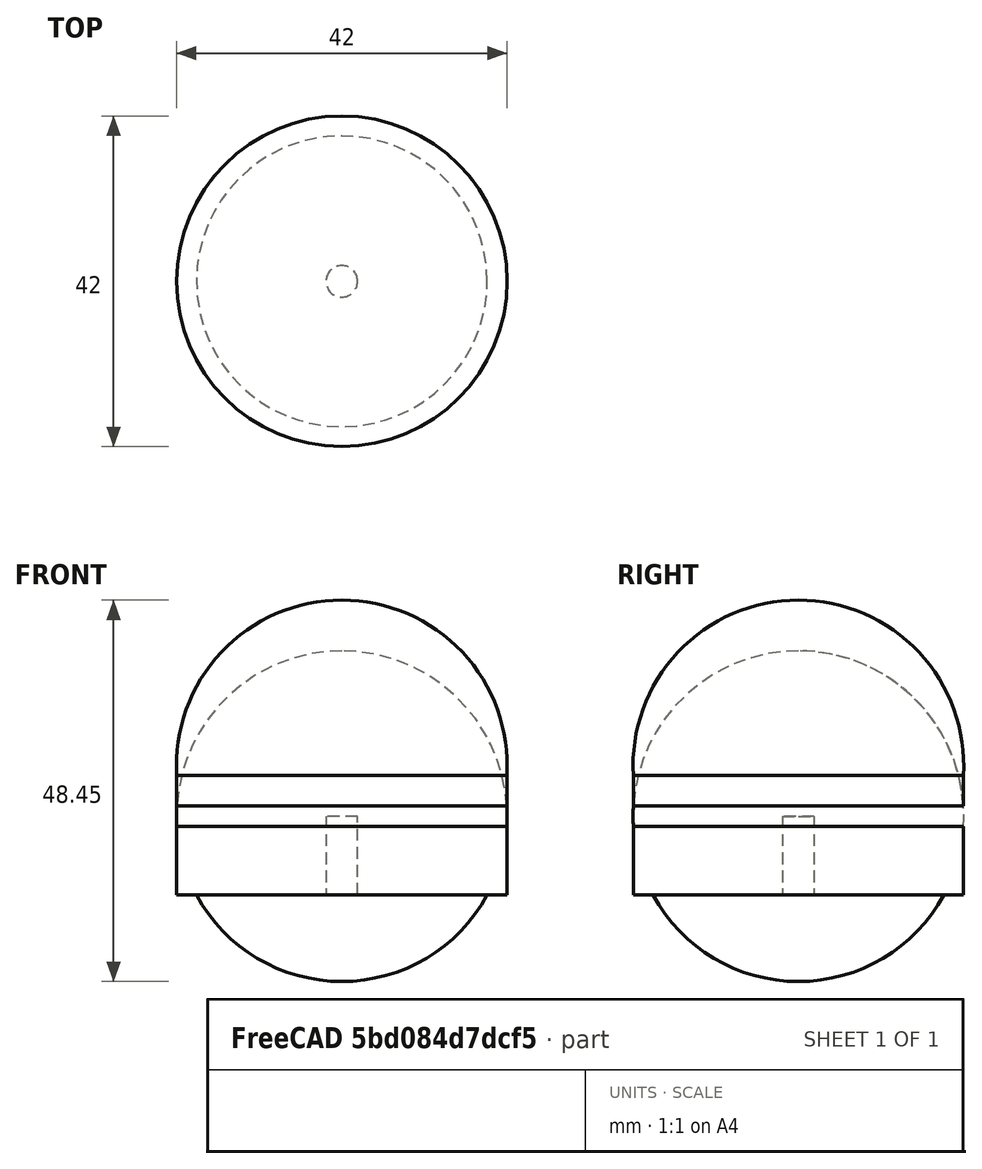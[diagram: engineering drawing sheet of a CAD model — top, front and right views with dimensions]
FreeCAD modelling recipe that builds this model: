
FCSTD DOCUMENT  (FreeCAD 1.0R39319 (Git))
Label: Final_looking_GOOD
License: Public Domain
LicenseURL: https://en.wikipedia.org/wiki/Public_domain
objects: Part::Cylinder×4, PartDesign::AdditiveSphere×2, Sketcher::SketchObject×1, PartDesign::Pad×1, PartDesign::Body×1, App::Part×1, Part::Cut×1
note: 17 computed .brp shape members not serialized (recipe doc carries the construction recipe); baked Part::Feature solids carry a one-line shape summary decoded from their .brp

FEATURE [Sketcher::SketchObject] Sketch
  ArcFitTolerance = 1e-06
  AttachmentSupport = -> [XY_Plane]
  FullyConstrained = false
  MakeInternals = false
  MapMode = 5
  sketch-geometry (2):
    g0: Circle CenterX=0 CenterY=0 CenterZ=0 NormalX=0 NormalY=0 NormalZ=1 AngleXU=0 Radius=20.96
    g1: Circle CenterX=-0.289044 CenterY=0 CenterZ=0 NormalX=0 NormalY=0 NormalZ=1 AngleXU=0 Radius=24.0036
  constraints (3):
    c: Diameter(g0) = 41.92
    c: Coincident(g0,g-1)
    c: PointOnObject(g1,g-1)
FEATURE [PartDesign::Pad] Pad
  Direction = (0,0,1)
  Length = 10
  Length2 = 10
  Profile = -> Sketch [Edge1]
  ReferenceAxis = -> Sketch [N_Axis]
  Refine = true
  Suppressed = false
  Type = 0
FEATURE [PartDesign::AdditiveSphere] Sphere
  Angle1 = -90
  Angle2 = 90
  Angle3 = 360
  AttacherType = Attacher::AttachEngine3D
  AttachmentSupport = -> [Pad]
  BaseFeature = -> Pad
  MapMode = 5
  Placement = pos=(0,0,10) rot=(0,0,1;0rad)
  Radius = 21
  Refine = true
  Suppressed = false
FEATURE [PartDesign::Body] Body
  AllowCompound = true
  Group = -> [Sketch,Pad,Sphere]
  Origin = -> Origin
  Tip = -> Sphere
FEATURE [PartDesign::AdditiveSphere] Sphere001
  Angle1 = -90
  Angle2 = 90
  Angle3 = 360
  AttacherType = Attacher::AttachEngine3D
  AttachmentSupport = -> [Pad]
  BaseFeature = -> Pad
  MapMode = 5
  Placement = pos=(0,0,10) rot=(0,0,1;0rad)
  Radius = 21
  Refine = true
  Suppressed = false
FEATURE [Part::Cylinder] Cylinder
  Angle = 360
  AttacherType = Attacher::AttachEngine3D
  FirstAngle = 0
  Height = 10
  Radius = 2
  SecondAngle = 0
FEATURE [Part::Cylinder] Cylinder001
  Angle = 360
  AttacherType = Attacher::AttachEngine3D
  FirstAngle = 0
  Height = 10
  Radius = 2
  SecondAngle = 0
FEATURE [Part::Cylinder] Cylinder002
  Angle = 360
  AttacherType = Attacher::AttachEngine3D
  FirstAngle = 0
  Height = 10
  Radius = 2
  SecondAngle = 0
FEATURE [Part::Cylinder] Cylinder003
  Angle = 360
  AttacherType = Attacher::AttachEngine3D
  FirstAngle = 0
  Height = 10
  Radius = 2
  SecondAngle = 0
FEATURE [App::Part] Part
  Group = -> [Body,Cylinder,Cylinder001,Cylinder002,Cylinder003]
  Origin = -> Origin001
  Placement = pos=(0,0,6.45) rot=(0,0,1;0rad)
FEATURE [Part::Cut] Cut
  Base = -> Part
  Refine = true
  Tool = -> Sphere001
